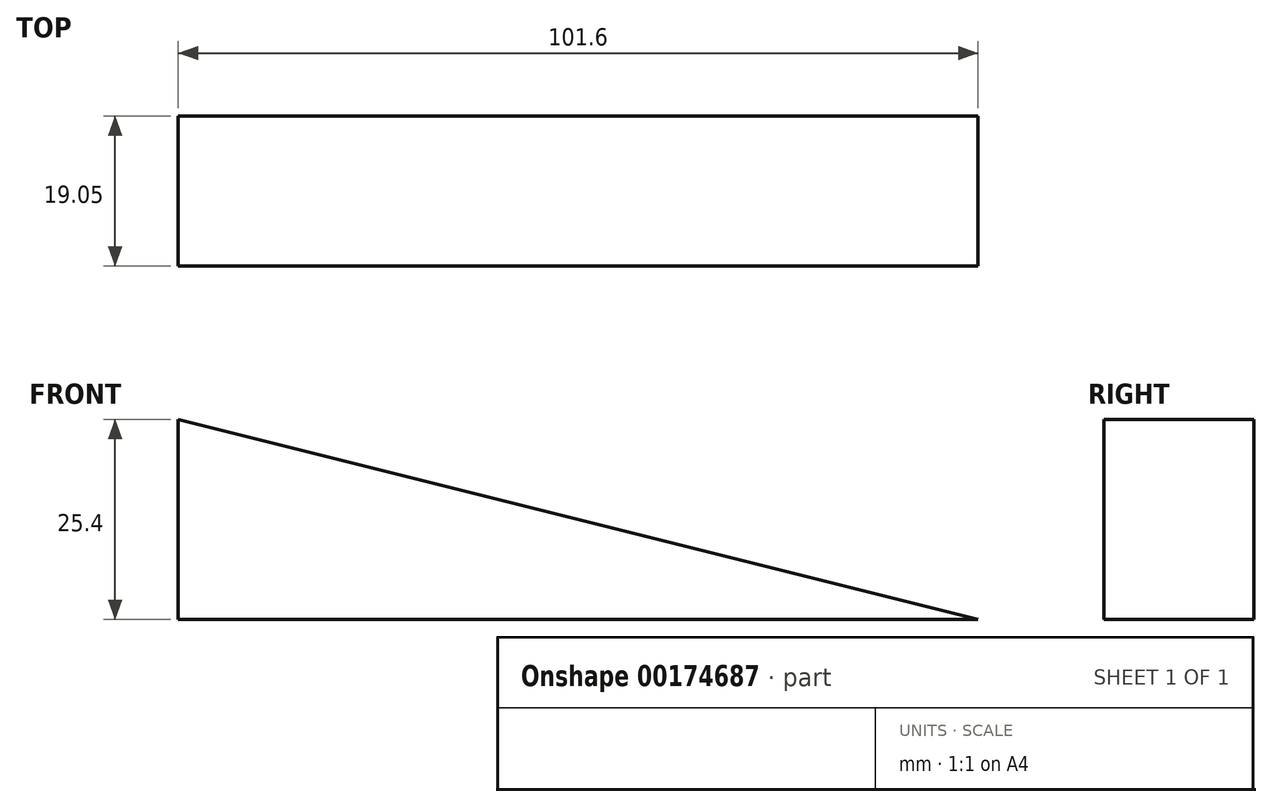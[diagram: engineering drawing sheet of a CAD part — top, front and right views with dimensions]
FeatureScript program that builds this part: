
annotation { "Feature Type Name" : "Feature", "Feature Type Description" : "" }
export const myFeature = defineFeature(function(context is Context, id is Id, definition is map)
    precondition{}
    {
        {
            var Q0;
            Q0=qCreatedBy(makeId("Front.planeOp"),FACE);
            var sketch = newSketch(context, id + "F0", { "sketchPlane" : qUnion([Q0])});
            skLineSegment(sketch, "E0.bottom", {"start": v(-75.76, 25.4) * mm, "end": v(25.84, 25.4) * mm});
            skLineSegment(sketch, "E0.top", {"start": v(-75.76, 0) * mm, "end": v(25.84, 0) * mm});
            skLineSegment(sketch, "E0.left", {"start": v(-75.76, 25.4) * mm, "end": v(-75.76, 0) * mm});
            skLineSegment(sketch, "E0.right", {"start": v(25.84, 25.4) * mm, "end": v(25.84, 0) * mm});
            skSolve(sketch);
        }
        {
            var Q0;
            Q0 = qSketchRegion(id + "F0", true);
            extrude(context, id + "F1", {"entities" : qUnion([Q0]), "depth" : 19.05 * mm});
        }
        {
            var Q0;
            Q0=makeQuery(id+"F1.opExtrude","CAP_FACE",FACE,{"disambiguationData":[OSD([sQuery(id+"F0.wireOp",EDGE,"E0.bottom"),sQuery(id+"F0.wireOp",EDGE,"E0.top"),sQuery(id+"F0.wireOp",EDGE,"E0.left"),sQuery(id+"F0.wireOp",EDGE,"E0.right")])],"isStart":false});
            var sketch = newSketch(context, id + "F2", { "sketchPlane" : qUnion([Q0])});
            skLineSegment(sketch, "E1", {"start": v(-75.76, 25.4) * mm, "end": v(25.84, 0) * mm});
            skSolve(sketch);
        }
        {
            var Q0;
            Q0=makeQuery(id+"F2.imprint","IMPRINT",FACE,{"disambiguationData":[TD([[makeQuery(id+"F2.imprint","IMPRINT",EDGE,{"derivedFrom":sQuery(id+"F2.wireOp",EDGE,"E1")}),1.0]])]});
            extrude(context, id + "F3", {"entities" : qUnion([Q0]), "operationType" : NewBodyOperationType.REMOVE, "endBound" : BoundingType.THROUGH_ALL, "oppositeDirection" : true, "depth" : 25.4 * mm});
        }
    });
